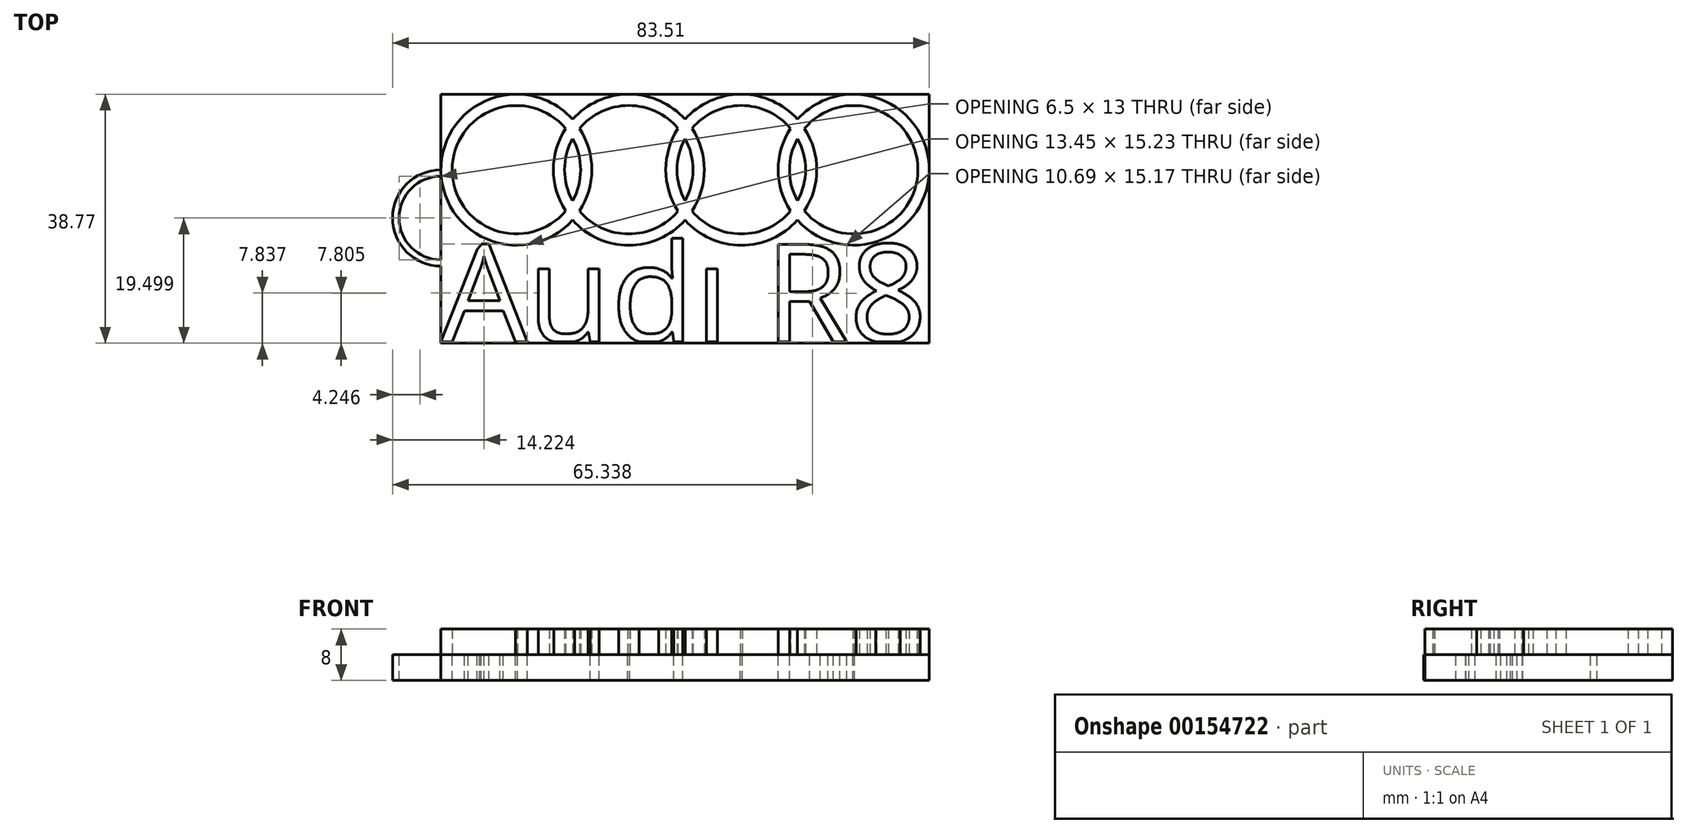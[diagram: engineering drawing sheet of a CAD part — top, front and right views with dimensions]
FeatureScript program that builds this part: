
annotation { "Feature Type Name" : "Feature", "Feature Type Description" : "" }
export const myFeature = defineFeature(function(context is Context, id is Id, definition is map)
    precondition{}
    {
        {
            var Q0;
            Q0=qCreatedBy(makeId("Top.planeOp"),FACE);
            var sketch = newSketch(context, id + "F0", { "sketchPlane" : qUnion([Q0])});
            skCircle(sketch, "E0", {"center": v(-42.08, 0) * mm, "radius": 10 * mm});
            skCircle(sketch, "E1", {"center": v(-24.58, 0) * mm, "radius": 10 * mm});
            skCircle(sketch, "E2", {"center": v(-7.08, 0) * mm, "radius": 10 * mm});
            skCircle(sketch, "E3", {"center": v(10.42, 0) * mm, "radius": 10 * mm});
            skCircle(sketch, "E4", {"center": v(-42.08, 0) * mm, "radius": 11.75 * mm});
            skCircle(sketch, "E5", {"center": v(-24.58, 0) * mm, "radius": 11.75 * mm});
            skCircle(sketch, "E6", {"center": v(-7.08, 0) * mm, "radius": 11.75 * mm});
            skCircle(sketch, "E7", {"center": v(10.42, 0) * mm, "radius": 11.75 * mm});
            skPoint(sketch, "E8.startSnap0", {"position": v(78.32, -3.69) * mm});
            skLineSegment(sketch, "E9", {"start": v(-57.65, 0) * mm, "end": v(52.35, 0) * mm});
            skLineSegment(sketch, "E10.bottom", {"start": v(-53.84, 11.75) * mm, "end": v(22.17, 11.75) * mm});
            skLineSegment(sketch, "E10.top", {"start": v(-53.84, -26.8) * mm, "end": v(22.17, -26.8) * mm});
            skLineSegment(sketch, "E10.left", {"start": v(-53.84, 11.75) * mm, "end": v(-53.84, -26.8) * mm});
            skLineSegment(sketch, "E10.right", {"start": v(22.17, 11.75) * mm, "end": v(22.17, -26.8) * mm});
            skText(sketch, "E11", { "text": "Audi R8", "fontName": "OpenSans-Regular.ttf"});
            skLineSegment(sketch, "E12.top", {"start": v(-53.84, -27.02) * mm, "end": v(22.17, -27.02) * mm});
            skLineSegment(sketch, "E12.left", {"start": v(-53.84, -26.8) * mm, "end": v(-53.84, -27.02) * mm});
            skLineSegment(sketch, "E12.right", {"start": v(22.17, -26.8) * mm, "end": v(22.17, -27.02) * mm});
            skCircle(sketch, "E13", {"center": v(-53.84, -7.52) * mm, "radius": 7.5 * mm});
            skCircle(sketch, "E14", {"center": v(-53.84, -7.52) * mm, "radius": 6.5 * mm});
            const initialGuessF0  = {"E11": [-0.05384, -0.0268, 1, 0, 0.0153]};
            skSetInitialGuess(sketch, initialGuessF0);
            skSolve(sketch);
        }
        {
            var Q0;
            Q0 = qSketchRegion(id + "F0", true);
            var Q1;
            {var subQ5=sQuery(id+"F0.wireOp",EDGE,"E5");var subQ6=sQuery(id+"F0.wireOp",EDGE,"E0");var subQ7=makeQuery(id+"F0.imprint","INTERSECT",VERTEX,{"disambiguationData":[OD(0.0)],"derivedFrom":[subQ6,subQ5]});Q1=makeQuery(id+"F0.imprint","IMPRINT",FACE,{"disambiguationData":[TD([[makeQuery(id+"F0.imprint","IMPRINT",EDGE,{"disambiguationData":[TD([[subQ7,-1.0]])],"derivedFrom":subQ6}),-1.0]])]});}
            var Q2;
            {var subQ0=sQuery(id+"F0.wireOp",EDGE,"E11.sketch_text.stroke-0");Q2=makeQuery(id+"F0.imprint","IMPRINT",FACE,{"disambiguationData":[TD([[makeQuery(id+"F0.imprint","IMPRINT",EDGE,{"derivedFrom":subQ0}),1.0]])]});}
            var Q3;
            {var subQ7=sQuery(id+"F0.wireOp",EDGE,"E14");var subQ10=sQuery(id+"F0.wireOp",EDGE,"E4");var subQ11=makeQuery(id+"F0.imprint","INTERSECT",VERTEX,{"disambiguationData":[OD(1.0)],"derivedFrom":[subQ10,subQ7]});Q3=makeQuery(id+"F0.imprint","IMPRINT",FACE,{"disambiguationData":[TD([[makeQuery(id+"F0.imprint","IMPRINT",EDGE,{"disambiguationData":[TD([[subQ11,-1.0]])],"derivedFrom":subQ10}),-1.0]])]});}
            var Q4;
            Q4=makeQuery(id+"F0.imprint","IMPRINT",FACE,{"disambiguationData":[TD([[makeQuery(id+"F0.imprint","IMPRINT",EDGE,{"derivedFrom":sQuery(id+"F0.wireOp",EDGE,"E11.sketch_text.stroke-84")}),-1.0]])]});
            var Q5;
            {var subQ0=sQuery(id+"F0.wireOp",EDGE,"E9");var subQ1=sQuery(id+"F0.wireOp",EDGE,"E2");var subQ2=makeQuery(id+"F0.imprint","INTERSECT",VERTEX,{"disambiguationData":[OD(0.0)],"derivedFrom":[subQ1,subQ0]});Q5=makeQuery(id+"F0.imprint","IMPRINT",FACE,{"disambiguationData":[TD([[makeQuery(id+"F0.imprint","IMPRINT",EDGE,{"disambiguationData":[TD([[subQ2,1.0]])],"derivedFrom":subQ1}),-1.0]])]});}
            var Q6;
            {var subQ0=sQuery(id+"F0.wireOp",EDGE,"E5");var subQ1=sQuery(id+"F0.wireOp",EDGE,"E0");var subQ2=makeQuery(id+"F0.imprint","INTERSECT",VERTEX,{"disambiguationData":[OD(1.0)],"derivedFrom":[subQ1,subQ0]});Q6=makeQuery(id+"F0.imprint","IMPRINT",FACE,{"disambiguationData":[TD([[makeQuery(id+"F0.imprint","IMPRINT",EDGE,{"disambiguationData":[TD([[subQ2,-1.0]])],"derivedFrom":subQ1}),-1.0]])]});}
            var Q7;
            {var subQ0=sQuery(id+"F0.wireOp",EDGE,"E3");var subQ1=sQuery(id+"F0.wireOp",EDGE,"E2");var subQ2=makeQuery(id+"F0.imprint","INTERSECT",VERTEX,{"disambiguationData":[OD(0.0)],"derivedFrom":[subQ1,subQ0]});Q7=makeQuery(id+"F0.imprint","IMPRINT",FACE,{"disambiguationData":[TD([[makeQuery(id+"F0.imprint","IMPRINT",EDGE,{"disambiguationData":[TD([[subQ2,1.0]])],"derivedFrom":subQ1}),1.0]])]});}
            var Q8;
            {var subQ0=sQuery(id+"F0.wireOp",EDGE,"E7");var subQ1=sQuery(id+"F0.wireOp",EDGE,"E2");var subQ2=makeQuery(id+"F0.imprint","INTERSECT",VERTEX,{"disambiguationData":[OD(1.0)],"derivedFrom":[subQ1,subQ0]});Q8=makeQuery(id+"F0.imprint","IMPRINT",FACE,{"disambiguationData":[TD([[makeQuery(id+"F0.imprint","IMPRINT",EDGE,{"disambiguationData":[TD([[subQ2,-1.0]])],"derivedFrom":subQ1}),1.0]])]});}
            var Q9;
            {var subQ0=sQuery(id+"F0.wireOp",EDGE,"E3");var subQ1=sQuery(id+"F0.wireOp",EDGE,"E2");var subQ2=makeQuery(id+"F0.imprint","INTERSECT",VERTEX,{"disambiguationData":[OD(0.0)],"derivedFrom":[subQ1,subQ0]});Q9=makeQuery(id+"F0.imprint","IMPRINT",FACE,{"disambiguationData":[TD([[makeQuery(id+"F0.imprint","IMPRINT",EDGE,{"disambiguationData":[TD([[subQ2,-1.0]])],"derivedFrom":subQ1}),-1.0]])]});}
            var Q10;
            {var subQ0=sQuery(id+"F0.wireOp",EDGE,"E14");var subQ1=sQuery(id+"F0.wireOp",EDGE,"E0");var subQ2=makeQuery(id+"F0.imprint","INTERSECT",VERTEX,{"disambiguationData":[OD(0.0)],"derivedFrom":[subQ1,subQ0]});Q10=makeQuery(id+"F0.imprint","IMPRINT",FACE,{"disambiguationData":[TD([[makeQuery(id+"F0.imprint","IMPRINT",EDGE,{"disambiguationData":[TD([[subQ2,-1.0]])],"derivedFrom":subQ1}),-1.0]])]});}
            var Q11;
            {var subQ0=sQuery(id+"F0.wireOp",EDGE,"E9");var subQ1=sQuery(id+"F0.wireOp",EDGE,"E1");var subQ2=makeQuery(id+"F0.imprint","INTERSECT",VERTEX,{"disambiguationData":[OD(0.0)],"derivedFrom":[subQ1,subQ0]});Q11=makeQuery(id+"F0.imprint","IMPRINT",FACE,{"disambiguationData":[TD([[makeQuery(id+"F0.imprint","IMPRINT",EDGE,{"disambiguationData":[TD([[subQ2,1.0]])],"derivedFrom":subQ1}),-1.0]])]});}
            var Q12;
            {var subQ0=sQuery(id+"F0.wireOp",EDGE,"E1");var subQ1=sQuery(id+"F0.wireOp",EDGE,"E0");var subQ2=makeQuery(id+"F0.imprint","INTERSECT",VERTEX,{"disambiguationData":[OD(0.0)],"derivedFrom":[subQ1,subQ0]});Q12=makeQuery(id+"F0.imprint","IMPRINT",FACE,{"disambiguationData":[TD([[makeQuery(id+"F0.imprint","IMPRINT",EDGE,{"disambiguationData":[TD([[subQ2,1.0]])],"derivedFrom":subQ1}),-1.0]])]});}
            var Q13;
            Q13=makeQuery(id+"F0.imprint","IMPRINT",FACE,{"disambiguationData":[TD([[makeQuery(id+"F0.imprint","IMPRINT",EDGE,{"derivedFrom":sQuery(id+"F0.wireOp",EDGE,"E11.sketch_text.stroke-77")}),1.0]])]});
            var Q14;
            {var subQ0=sQuery(id+"F0.wireOp",EDGE,"E5");var subQ1=sQuery(id+"F0.wireOp",EDGE,"E2");var subQ2=makeQuery(id+"F0.imprint","INTERSECT",VERTEX,{"disambiguationData":[OD(1.0)],"derivedFrom":[subQ1,subQ0]});Q14=makeQuery(id+"F0.imprint","IMPRINT",FACE,{"disambiguationData":[TD([[makeQuery(id+"F0.imprint","IMPRINT",EDGE,{"disambiguationData":[TD([[subQ2,-1.0]])],"derivedFrom":subQ1}),1.0]])]});}
            var Q15;
            {var subQ0=sQuery(id+"F0.wireOp",EDGE,"E9");var subQ1=sQuery(id+"F0.wireOp",EDGE,"E0");var subQ2=makeQuery(id+"F0.imprint","INTERSECT",VERTEX,{"disambiguationData":[OD(0.0)],"derivedFrom":[subQ1,subQ0]});Q15=makeQuery(id+"F0.imprint","IMPRINT",FACE,{"disambiguationData":[TD([[makeQuery(id+"F0.imprint","IMPRINT",EDGE,{"disambiguationData":[TD([[subQ2,1.0]])],"derivedFrom":subQ1}),-1.0]])]});}
            var Q16;
            {var subQ0=sQuery(id+"F0.wireOp",EDGE,"E3");var subQ1=sQuery(id+"F0.wireOp",EDGE,"E2");var subQ2=makeQuery(id+"F0.imprint","INTERSECT",VERTEX,{"disambiguationData":[OD(0.0)],"derivedFrom":[subQ1,subQ0]});Q16=makeQuery(id+"F0.imprint","IMPRINT",FACE,{"disambiguationData":[TD([[makeQuery(id+"F0.imprint","IMPRINT",EDGE,{"disambiguationData":[TD([[subQ2,1.0]])],"derivedFrom":subQ1}),-1.0]])]});}
            var Q17;
            {var subQ0=sQuery(id+"F0.wireOp",EDGE,"E1");var subQ1=sQuery(id+"F0.wireOp",EDGE,"E0");var subQ2=makeQuery(id+"F0.imprint","INTERSECT",VERTEX,{"disambiguationData":[OD(0.0)],"derivedFrom":[subQ1,subQ0]});Q17=makeQuery(id+"F0.imprint","IMPRINT",FACE,{"disambiguationData":[TD([[makeQuery(id+"F0.imprint","IMPRINT",EDGE,{"disambiguationData":[TD([[subQ2,-1.0]])],"derivedFrom":subQ1}),-1.0]])]});}
            var Q18;
            {var subQ0=sQuery(id+"F0.wireOp",EDGE,"E2");var subQ1=sQuery(id+"F0.wireOp",EDGE,"E1");var subQ2=makeQuery(id+"F0.imprint","INTERSECT",VERTEX,{"disambiguationData":[OD(0.0)],"derivedFrom":[subQ1,subQ0]});Q18=makeQuery(id+"F0.imprint","IMPRINT",FACE,{"disambiguationData":[TD([[makeQuery(id+"F0.imprint","IMPRINT",EDGE,{"disambiguationData":[TD([[subQ2,1.0]])],"derivedFrom":subQ1}),1.0]])]});}
            var Q19;
            {var subQ0=sQuery(id+"F0.wireOp",EDGE,"E9");var subQ1=sQuery(id+"F0.wireOp",EDGE,"E2");var subQ2=makeQuery(id+"F0.imprint","INTERSECT",VERTEX,{"disambiguationData":[OD(0.0)],"derivedFrom":[subQ1,subQ0]});Q19=makeQuery(id+"F0.imprint","IMPRINT",FACE,{"disambiguationData":[TD([[makeQuery(id+"F0.imprint","IMPRINT",EDGE,{"disambiguationData":[TD([[subQ2,1.0]])],"derivedFrom":subQ1}),1.0]])]});}
            var Q20;
            Q20=makeQuery(id+"F0.imprint","IMPRINT",FACE,{"disambiguationData":[TD([[makeQuery(id+"F0.imprint","IMPRINT",EDGE,{"derivedFrom":sQuery(id+"F0.wireOp",EDGE,"E11.sketch_text.stroke-99")}),1.0]])]});
            var Q21;
            {var subQ0=sQuery(id+"F0.wireOp",EDGE,"E13");var subQ1=sQuery(id+"F0.wireOp",EDGE,"E10.left");var subQ2=makeQuery(id+"F0.imprint","INTERSECT",VERTEX,{"disambiguationData":[OD(0.0)],"derivedFrom":[subQ1,subQ0]});Q21=makeQuery(id+"F0.imprint","IMPRINT",FACE,{"disambiguationData":[TD([[makeQuery(id+"F0.imprint","IMPRINT",EDGE,{"disambiguationData":[TD([[subQ2,-1.0]])],"derivedFrom":subQ1}),-1.0]])]});}
            var Q22;
            Q22=makeQuery(id+"F0.imprint","IMPRINT",FACE,{"disambiguationData":[TD([[makeQuery(id+"F0.imprint","IMPRINT",EDGE,{"derivedFrom":sQuery(id+"F0.wireOp",EDGE,"E11.sketch_text.stroke-58")}),-1.0]])]});
            var Q23;
            {var subQ0=sQuery(id+"F0.wireOp",EDGE,"E11.sketch_text.stroke-55");Q23=makeQuery(id+"F0.imprint","IMPRINT",FACE,{"disambiguationData":[TD([[makeQuery(id+"F0.imprint","IMPRINT",EDGE,{"derivedFrom":subQ0}),-1.0]])]});}
            var Q24;
            {var subQ0=sQuery(id+"F0.wireOp",EDGE,"E9");var subQ1=sQuery(id+"F0.wireOp",EDGE,"E3");var subQ2=makeQuery(id+"F0.imprint","INTERSECT",VERTEX,{"disambiguationData":[OD(0.0)],"derivedFrom":[subQ1,subQ0]});Q24=makeQuery(id+"F0.imprint","IMPRINT",FACE,{"disambiguationData":[TD([[makeQuery(id+"F0.imprint","IMPRINT",EDGE,{"disambiguationData":[TD([[subQ2,1.0]])],"derivedFrom":subQ1}),-1.0]])]});}
            var Q25;
            {var subQ0=sQuery(id+"F0.wireOp",EDGE,"E2");var subQ1=sQuery(id+"F0.wireOp",EDGE,"E1");var subQ2=makeQuery(id+"F0.imprint","INTERSECT",VERTEX,{"disambiguationData":[OD(0.0)],"derivedFrom":[subQ1,subQ0]});Q25=makeQuery(id+"F0.imprint","IMPRINT",FACE,{"disambiguationData":[TD([[makeQuery(id+"F0.imprint","IMPRINT",EDGE,{"disambiguationData":[TD([[subQ2,-1.0]])],"derivedFrom":subQ1}),1.0]])]});}
            var Q26;
            {var subQ2=sQuery(id+"F0.wireOp",EDGE,"E11.sketch_text.stroke-30");Q26=makeQuery(id+"F0.imprint","IMPRINT",FACE,{"disambiguationData":[TD([[makeQuery(id+"F0.imprint","IMPRINT",EDGE,{"derivedFrom":subQ2}),-1.0]])]});}
            var Q27;
            {var subQ0=sQuery(id+"F0.wireOp",EDGE,"E9");var subQ1=sQuery(id+"F0.wireOp",EDGE,"E0");var subQ2=makeQuery(id+"F0.imprint","INTERSECT",VERTEX,{"disambiguationData":[OD(0.0)],"derivedFrom":[subQ1,subQ0]});Q27=makeQuery(id+"F0.imprint","IMPRINT",FACE,{"disambiguationData":[TD([[makeQuery(id+"F0.imprint","IMPRINT",EDGE,{"disambiguationData":[TD([[subQ2,1.0]])],"derivedFrom":subQ1}),1.0]])]});}
            var Q28;
            {var subQ0=sQuery(id+"F0.wireOp",EDGE,"E6");var subQ1=sQuery(id+"F0.wireOp",EDGE,"E3");var subQ2=makeQuery(id+"F0.imprint","INTERSECT",VERTEX,{"disambiguationData":[OD(0.0)],"derivedFrom":[subQ1,subQ0]});Q28=makeQuery(id+"F0.imprint","IMPRINT",FACE,{"disambiguationData":[TD([[makeQuery(id+"F0.imprint","IMPRINT",EDGE,{"disambiguationData":[TD([[subQ2,1.0]])],"derivedFrom":subQ1}),1.0]])]});}
            var Q29;
            {var subQ0=sQuery(id+"F0.wireOp",EDGE,"E14");var subQ1=sQuery(id+"F0.wireOp",EDGE,"E0");var subQ2=makeQuery(id+"F0.imprint","INTERSECT",VERTEX,{"disambiguationData":[OD(1.0)],"derivedFrom":[subQ1,subQ0]});Q29=makeQuery(id+"F0.imprint","IMPRINT",FACE,{"disambiguationData":[TD([[makeQuery(id+"F0.imprint","IMPRINT",EDGE,{"disambiguationData":[TD([[subQ2,-1.0]])],"derivedFrom":subQ1}),-1.0]])]});}
            var Q30;
            {var subQ0=sQuery(id+"F0.wireOp",EDGE,"E5");var subQ1=sQuery(id+"F0.wireOp",EDGE,"E0");var subQ2=makeQuery(id+"F0.imprint","INTERSECT",VERTEX,{"disambiguationData":[OD(1.0)],"derivedFrom":[subQ1,subQ0]});Q30=makeQuery(id+"F0.imprint","IMPRINT",FACE,{"disambiguationData":[TD([[makeQuery(id+"F0.imprint","IMPRINT",EDGE,{"disambiguationData":[TD([[subQ2,-1.0]])],"derivedFrom":subQ1}),1.0]])]});}
            var Q31;
            {var subQ0=sQuery(id+"F0.wireOp",EDGE,"E5");var subQ1=sQuery(id+"F0.wireOp",EDGE,"E0");var subQ2=makeQuery(id+"F0.imprint","INTERSECT",VERTEX,{"disambiguationData":[OD(0.0)],"derivedFrom":[subQ1,subQ0]});Q31=makeQuery(id+"F0.imprint","IMPRINT",FACE,{"disambiguationData":[TD([[makeQuery(id+"F0.imprint","IMPRINT",EDGE,{"disambiguationData":[TD([[subQ2,-1.0]])],"derivedFrom":subQ1}),1.0]])]});}
            var Q32;
            {var subQ1=sQuery(id+"F0.wireOp",EDGE,"E10.left");var subQ3=sQuery(id+"F0.wireOp",EDGE,"E13");var subQ4=makeQuery(id+"F0.imprint","INTERSECT",VERTEX,{"disambiguationData":[OD(1.0)],"derivedFrom":[subQ1,subQ3]});Q32=makeQuery(id+"F0.imprint","IMPRINT",FACE,{"disambiguationData":[TD([[makeQuery(id+"F0.imprint","IMPRINT",EDGE,{"disambiguationData":[TD([[subQ4,-1.0]])],"derivedFrom":subQ3}),-1.0]])]});}
            var Q33;
            {var subQ0=sQuery(id+"F0.wireOp",EDGE,"E2");var subQ1=sQuery(id+"F0.wireOp",EDGE,"E1");var subQ2=makeQuery(id+"F0.imprint","INTERSECT",VERTEX,{"disambiguationData":[OD(0.0)],"derivedFrom":[subQ1,subQ0]});Q33=makeQuery(id+"F0.imprint","IMPRINT",FACE,{"disambiguationData":[TD([[makeQuery(id+"F0.imprint","IMPRINT",EDGE,{"disambiguationData":[TD([[subQ2,1.0]])],"derivedFrom":subQ1}),-1.0]])]});}
            var Q34;
            {var subQ0=sQuery(id+"F0.wireOp",EDGE,"E9");var subQ1=sQuery(id+"F0.wireOp",EDGE,"E3");var subQ2=makeQuery(id+"F0.imprint","INTERSECT",VERTEX,{"disambiguationData":[OD(0.0)],"derivedFrom":[subQ1,subQ0]});Q34=makeQuery(id+"F0.imprint","IMPRINT",FACE,{"disambiguationData":[TD([[makeQuery(id+"F0.imprint","IMPRINT",EDGE,{"disambiguationData":[TD([[subQ2,1.0]])],"derivedFrom":subQ1}),1.0]])]});}
            var Q35;
            {var subQ0=sQuery(id+"F0.wireOp",EDGE,"E14");var subQ1=sQuery(id+"F0.wireOp",EDGE,"E4");var subQ2=makeQuery(id+"F0.imprint","INTERSECT",VERTEX,{"disambiguationData":[OD(0.0)],"derivedFrom":[subQ1,subQ0]});Q35=makeQuery(id+"F0.imprint","IMPRINT",FACE,{"disambiguationData":[TD([[makeQuery(id+"F0.imprint","IMPRINT",EDGE,{"disambiguationData":[TD([[subQ2,-1.0]])],"derivedFrom":subQ1}),-1.0]])]});}
            var Q36;
            {var subQ0=sQuery(id+"F0.wireOp",EDGE,"E13");var subQ1=sQuery(id+"F0.wireOp",EDGE,"E0");var subQ2=makeQuery(id+"F0.imprint","INTERSECT",VERTEX,{"disambiguationData":[OD(0.0)],"derivedFrom":[subQ1,subQ0]});Q36=makeQuery(id+"F0.imprint","IMPRINT",FACE,{"disambiguationData":[TD([[makeQuery(id+"F0.imprint","IMPRINT",EDGE,{"disambiguationData":[TD([[subQ2,-1.0]])],"derivedFrom":subQ1}),1.0]])]});}
            var Q37;
            {var subQ0=sQuery(id+"F0.wireOp",EDGE,"E1");var subQ1=sQuery(id+"F0.wireOp",EDGE,"E0");var subQ2=makeQuery(id+"F0.imprint","INTERSECT",VERTEX,{"disambiguationData":[OD(0.0)],"derivedFrom":[subQ1,subQ0]});Q37=makeQuery(id+"F0.imprint","IMPRINT",FACE,{"disambiguationData":[TD([[makeQuery(id+"F0.imprint","IMPRINT",EDGE,{"disambiguationData":[TD([[subQ2,1.0]])],"derivedFrom":subQ1}),1.0]])]});}
            var Q38;
            Q38=makeQuery(id+"F0.imprint","IMPRINT",FACE,{"disambiguationData":[TD([[makeQuery(id+"F0.imprint","IMPRINT",EDGE,{"derivedFrom":sQuery(id+"F0.wireOp",EDGE,"E11.sketch_text.stroke-107")}),1.0]])]});
            var Q39;
            Q39=makeQuery(id+"F0.imprint","IMPRINT",FACE,{"disambiguationData":[TD([[makeQuery(id+"F0.imprint","IMPRINT",EDGE,{"derivedFrom":sQuery(id+"F0.wireOp",EDGE,"E11.sketch_text.stroke-45")}),1.0]])]});
            var Q40;
            {var subQ0=sQuery(id+"F0.wireOp",EDGE,"E6");var subQ1=sQuery(id+"F0.wireOp",EDGE,"E3");var subQ2=makeQuery(id+"F0.imprint","INTERSECT",VERTEX,{"disambiguationData":[OD(0.0)],"derivedFrom":[subQ1,subQ0]});Q40=makeQuery(id+"F0.imprint","IMPRINT",FACE,{"disambiguationData":[TD([[makeQuery(id+"F0.imprint","IMPRINT",EDGE,{"disambiguationData":[TD([[subQ2,1.0]])],"derivedFrom":subQ1}),-1.0]])]});}
            var Q41;
            {var subQ0=sQuery(id+"F0.wireOp",EDGE,"E4");var subQ1=sQuery(id+"F0.wireOp",EDGE,"E1");var subQ2=makeQuery(id+"F0.imprint","INTERSECT",VERTEX,{"disambiguationData":[OD(1.0)],"derivedFrom":[subQ1,subQ0]});Q41=makeQuery(id+"F0.imprint","IMPRINT",FACE,{"disambiguationData":[TD([[makeQuery(id+"F0.imprint","IMPRINT",EDGE,{"disambiguationData":[TD([[subQ2,-1.0]])],"derivedFrom":subQ1}),1.0]])]});}
            var Q42;
            {var subQ0=sQuery(id+"F0.wireOp",EDGE,"E7");var subQ1=sQuery(id+"F0.wireOp",EDGE,"E2");var subQ2=makeQuery(id+"F0.imprint","INTERSECT",VERTEX,{"disambiguationData":[OD(1.0)],"derivedFrom":[subQ1,subQ0]});Q42=makeQuery(id+"F0.imprint","IMPRINT",FACE,{"disambiguationData":[TD([[makeQuery(id+"F0.imprint","IMPRINT",EDGE,{"disambiguationData":[TD([[subQ2,-1.0]])],"derivedFrom":subQ1}),-1.0]])]});}
            var Q43;
            {var subQ0=sQuery(id+"F0.wireOp",EDGE,"E6");var subQ1=sQuery(id+"F0.wireOp",EDGE,"E1");var subQ2=makeQuery(id+"F0.imprint","INTERSECT",VERTEX,{"disambiguationData":[OD(1.0)],"derivedFrom":[subQ1,subQ0]});Q43=makeQuery(id+"F0.imprint","IMPRINT",FACE,{"disambiguationData":[TD([[makeQuery(id+"F0.imprint","IMPRINT",EDGE,{"disambiguationData":[TD([[subQ2,-1.0]])],"derivedFrom":subQ1}),-1.0]])]});}
            var Q44;
            {var subQ0=sQuery(id+"F0.wireOp",EDGE,"E5");var subQ1=sQuery(id+"F0.wireOp",EDGE,"E2");var subQ2=makeQuery(id+"F0.imprint","INTERSECT",VERTEX,{"disambiguationData":[OD(1.0)],"derivedFrom":[subQ1,subQ0]});Q44=makeQuery(id+"F0.imprint","IMPRINT",FACE,{"disambiguationData":[TD([[makeQuery(id+"F0.imprint","IMPRINT",EDGE,{"disambiguationData":[TD([[subQ2,-1.0]])],"derivedFrom":subQ1}),-1.0]])]});}
            var Q45;
            {var subQ4=sQuery(id+"F0.wireOp",EDGE,"E11.sketch_text.stroke-22");Q45=makeQuery(id+"F0.imprint","IMPRINT",FACE,{"disambiguationData":[TD([[makeQuery(id+"F0.imprint","IMPRINT",EDGE,{"derivedFrom":subQ4}),1.0]])]});}
            var Q46;
            {var subQ0=sQuery(id+"F0.wireOp",EDGE,"E13");var subQ1=sQuery(id+"F0.wireOp",EDGE,"E0");var subQ2=makeQuery(id+"F0.imprint","INTERSECT",VERTEX,{"disambiguationData":[OD(1.0)],"derivedFrom":[subQ1,subQ0]});Q46=makeQuery(id+"F0.imprint","IMPRINT",FACE,{"disambiguationData":[TD([[makeQuery(id+"F0.imprint","IMPRINT",EDGE,{"disambiguationData":[TD([[subQ2,-1.0]])],"derivedFrom":subQ1}),-1.0]])]});}
            var Q47;
            {var subQ0=sQuery(id+"F0.wireOp",EDGE,"E10.bottom");var subQ1=sQuery(id+"F0.wireOp",EDGE,"E7");var subQ2=makeQuery(id+"F0.imprint","INTERSECT",VERTEX,{"disambiguationData":[OD(0.0)],"derivedFrom":[subQ1,subQ0]});Q47=makeQuery(id+"F0.imprint","IMPRINT",FACE,{"disambiguationData":[TD([[makeQuery(id+"F0.imprint","IMPRINT",EDGE,{"disambiguationData":[TD([[subQ2,1.0]])],"derivedFrom":subQ1}),-1.0]])]});}
            var Q48;
            {var subQ0=sQuery(id+"F0.wireOp",EDGE,"E14");var subQ1=sQuery(id+"F0.wireOp",EDGE,"E0");var subQ2=makeQuery(id+"F0.imprint","INTERSECT",VERTEX,{"disambiguationData":[OD(0.0)],"derivedFrom":[subQ1,subQ0]});Q48=makeQuery(id+"F0.imprint","IMPRINT",FACE,{"disambiguationData":[TD([[makeQuery(id+"F0.imprint","IMPRINT",EDGE,{"disambiguationData":[TD([[subQ2,-1.0]])],"derivedFrom":subQ1}),1.0]])]});}
            var Q49;
            {var subQ0=sQuery(id+"F0.wireOp",EDGE,"E3");var subQ1=sQuery(id+"F0.wireOp",EDGE,"E2");var subQ2=makeQuery(id+"F0.imprint","INTERSECT",VERTEX,{"disambiguationData":[OD(0.0)],"derivedFrom":[subQ1,subQ0]});Q49=makeQuery(id+"F0.imprint","IMPRINT",FACE,{"disambiguationData":[TD([[makeQuery(id+"F0.imprint","IMPRINT",EDGE,{"disambiguationData":[TD([[subQ2,-1.0]])],"derivedFrom":subQ1}),1.0]])]});}
            var Q50;
            {var subQ0=sQuery(id+"F0.wireOp",EDGE,"E6");var subQ1=sQuery(id+"F0.wireOp",EDGE,"E1");var subQ2=makeQuery(id+"F0.imprint","INTERSECT",VERTEX,{"disambiguationData":[OD(0.0)],"derivedFrom":[subQ1,subQ0]});Q50=makeQuery(id+"F0.imprint","IMPRINT",FACE,{"disambiguationData":[TD([[makeQuery(id+"F0.imprint","IMPRINT",EDGE,{"disambiguationData":[TD([[subQ2,-1.0]])],"derivedFrom":subQ1}),1.0]])]});}
            var Q51;
            {var subQ0=sQuery(id+"F0.wireOp",EDGE,"E11.sketch_text.stroke-66");Q51=makeQuery(id+"F0.imprint","IMPRINT",FACE,{"disambiguationData":[TD([[makeQuery(id+"F0.imprint","IMPRINT",EDGE,{"derivedFrom":subQ0}),1.0]])]});}
            var Q52;
            {var subQ0=sQuery(id+"F0.wireOp",EDGE,"E7");var subQ1=sQuery(id+"F0.wireOp",EDGE,"E2");var subQ2=makeQuery(id+"F0.imprint","INTERSECT",VERTEX,{"disambiguationData":[OD(0.0)],"derivedFrom":[subQ1,subQ0]});Q52=makeQuery(id+"F0.imprint","IMPRINT",FACE,{"disambiguationData":[TD([[makeQuery(id+"F0.imprint","IMPRINT",EDGE,{"disambiguationData":[TD([[subQ2,-1.0]])],"derivedFrom":subQ1}),1.0]])]});}
            var Q53;
            {var subQ0=sQuery(id+"F0.wireOp",EDGE,"E6");var subQ1=sQuery(id+"F0.wireOp",EDGE,"E1");var subQ2=makeQuery(id+"F0.imprint","INTERSECT",VERTEX,{"disambiguationData":[OD(1.0)],"derivedFrom":[subQ1,subQ0]});Q53=makeQuery(id+"F0.imprint","IMPRINT",FACE,{"disambiguationData":[TD([[makeQuery(id+"F0.imprint","IMPRINT",EDGE,{"disambiguationData":[TD([[subQ2,-1.0]])],"derivedFrom":subQ1}),1.0]])]});}
            var Q54;
            {var subQ0=sQuery(id+"F0.wireOp",EDGE,"E9");var subQ1=sQuery(id+"F0.wireOp",EDGE,"E1");var subQ2=makeQuery(id+"F0.imprint","INTERSECT",VERTEX,{"disambiguationData":[OD(0.0)],"derivedFrom":[subQ1,subQ0]});Q54=makeQuery(id+"F0.imprint","IMPRINT",FACE,{"disambiguationData":[TD([[makeQuery(id+"F0.imprint","IMPRINT",EDGE,{"disambiguationData":[TD([[subQ2,1.0]])],"derivedFrom":subQ1}),1.0]])]});}
            var Q55;
            {var subQ0=sQuery(id+"F0.wireOp",EDGE,"E1");var subQ1=sQuery(id+"F0.wireOp",EDGE,"E0");var subQ2=makeQuery(id+"F0.imprint","INTERSECT",VERTEX,{"disambiguationData":[OD(0.0)],"derivedFrom":[subQ1,subQ0]});Q55=makeQuery(id+"F0.imprint","IMPRINT",FACE,{"disambiguationData":[TD([[makeQuery(id+"F0.imprint","IMPRINT",EDGE,{"disambiguationData":[TD([[subQ2,-1.0]])],"derivedFrom":subQ1}),1.0]])]});}
            var Q56;
            {var subQ0=sQuery(id+"F0.wireOp",EDGE,"E10.bottom");var subQ1=sQuery(id+"F0.wireOp",EDGE,"E6");var subQ2=makeQuery(id+"F0.imprint","INTERSECT",VERTEX,{"disambiguationData":[OD(0.0)],"derivedFrom":[subQ1,subQ0]});Q56=makeQuery(id+"F0.imprint","IMPRINT",FACE,{"disambiguationData":[TD([[makeQuery(id+"F0.imprint","IMPRINT",EDGE,{"disambiguationData":[TD([[subQ2,1.0]])],"derivedFrom":subQ1}),-1.0]])]});}
            var Q57;
            {var subQ0=sQuery(id+"F0.wireOp",EDGE,"E13");var subQ1=sQuery(id+"F0.wireOp",EDGE,"E0");var subQ2=makeQuery(id+"F0.imprint","INTERSECT",VERTEX,{"disambiguationData":[OD(0.0)],"derivedFrom":[subQ1,subQ0]});Q57=makeQuery(id+"F0.imprint","IMPRINT",FACE,{"disambiguationData":[TD([[makeQuery(id+"F0.imprint","IMPRINT",EDGE,{"disambiguationData":[TD([[subQ2,-1.0]])],"derivedFrom":subQ1}),-1.0]])]});}
            var Q58;
            {var subQ5=sQuery(id+"F0.wireOp",EDGE,"E11.sketch_text.stroke-0");Q58=makeQuery(id+"F0.imprint","IMPRINT",FACE,{"disambiguationData":[TD([[makeQuery(id+"F0.imprint","IMPRINT",EDGE,{"derivedFrom":subQ5}),-1.0]])]});}
            var Q59;
            Q59=makeQuery(id+"F0.imprint","IMPRINT",FACE,{"disambiguationData":[TD([[makeQuery(id+"F0.imprint","IMPRINT",EDGE,{"derivedFrom":sQuery(id+"F0.wireOp",EDGE,"E11.sketch_text.stroke-8")}),1.0]])]});
            var Q60;
            {var subQ3=sQuery(id+"F0.wireOp",EDGE,"E7");var subQ5=sQuery(id+"F0.wireOp",EDGE,"E2");var subQ6=makeQuery(id+"F0.imprint","INTERSECT",VERTEX,{"disambiguationData":[OD(0.0)],"derivedFrom":[subQ5,subQ3]});Q60=makeQuery(id+"F0.imprint","IMPRINT",FACE,{"disambiguationData":[TD([[makeQuery(id+"F0.imprint","IMPRINT",EDGE,{"disambiguationData":[TD([[subQ6,-1.0]])],"derivedFrom":subQ5}),-1.0]])]});}
            var Q61;
            {var subQ0=sQuery(id+"F0.wireOp",EDGE,"E4");var subQ1=sQuery(id+"F0.wireOp",EDGE,"E1");var subQ2=makeQuery(id+"F0.imprint","INTERSECT",VERTEX,{"disambiguationData":[OD(1.0)],"derivedFrom":[subQ1,subQ0]});Q61=makeQuery(id+"F0.imprint","IMPRINT",FACE,{"disambiguationData":[TD([[makeQuery(id+"F0.imprint","IMPRINT",EDGE,{"disambiguationData":[TD([[subQ2,-1.0]])],"derivedFrom":subQ1}),-1.0]])]});}
            var Q62;
            {var subQ6=sQuery(id+"F0.wireOp",EDGE,"E6");var subQ8=sQuery(id+"F0.wireOp",EDGE,"E1");var subQ10=makeQuery(id+"F0.imprint","INTERSECT",VERTEX,{"disambiguationData":[OD(0.0)],"derivedFrom":[subQ8,subQ6]});Q62=makeQuery(id+"F0.imprint","IMPRINT",FACE,{"disambiguationData":[TD([[makeQuery(id+"F0.imprint","IMPRINT",EDGE,{"disambiguationData":[TD([[subQ10,-1.0]])],"derivedFrom":subQ8}),-1.0]])]});}
            var Q63;
            {var subQ0=sQuery(id+"F0.wireOp",EDGE,"E2");var subQ1=sQuery(id+"F0.wireOp",EDGE,"E1");var subQ2=makeQuery(id+"F0.imprint","INTERSECT",VERTEX,{"disambiguationData":[OD(0.0)],"derivedFrom":[subQ1,subQ0]});Q63=makeQuery(id+"F0.imprint","IMPRINT",FACE,{"disambiguationData":[TD([[makeQuery(id+"F0.imprint","IMPRINT",EDGE,{"disambiguationData":[TD([[subQ2,-1.0]])],"derivedFrom":subQ1}),-1.0]])]});}
            var Q64;
            {var subQ0=sQuery(id+"F0.wireOp",EDGE,"E10.bottom");var subQ1=sQuery(id+"F0.wireOp",EDGE,"E5");var subQ2=makeQuery(id+"F0.imprint","INTERSECT",VERTEX,{"disambiguationData":[OD(0.0)],"derivedFrom":[subQ1,subQ0]});Q64=makeQuery(id+"F0.imprint","IMPRINT",FACE,{"disambiguationData":[TD([[makeQuery(id+"F0.imprint","IMPRINT",EDGE,{"disambiguationData":[TD([[subQ2,1.0]])],"derivedFrom":subQ1}),-1.0]])]});}
            var Q65;
            {var subQ0=sQuery(id+"F0.wireOp",EDGE,"E11.sketch_text.stroke-30");Q65=makeQuery(id+"F0.imprint","IMPRINT",FACE,{"disambiguationData":[TD([[makeQuery(id+"F0.imprint","IMPRINT",EDGE,{"derivedFrom":subQ0}),1.0]])]});}
            var Q66;
            {var subQ0=sQuery(id+"F0.wireOp",EDGE,"E10.bottom");var subQ1=sQuery(id+"F0.wireOp",EDGE,"E4");var subQ2=makeQuery(id+"F0.imprint","INTERSECT",VERTEX,{"disambiguationData":[OD(1.0)],"derivedFrom":[subQ1,subQ0]});Q66=makeQuery(id+"F0.imprint","IMPRINT",FACE,{"disambiguationData":[TD([[makeQuery(id+"F0.imprint","IMPRINT",EDGE,{"disambiguationData":[TD([[subQ2,-1.0]])],"derivedFrom":subQ1}),-1.0]])]});}
            var Q67;
            {var subQ0=sQuery(id+"F0.wireOp",EDGE,"E9");var subQ1=sQuery(id+"F0.wireOp",EDGE,"E0");var subQ2=makeQuery(id+"F0.imprint","INTERSECT",VERTEX,{"disambiguationData":[OD(1.0)],"derivedFrom":[subQ1,subQ0]});Q67=makeQuery(id+"F0.imprint","IMPRINT",FACE,{"disambiguationData":[TD([[makeQuery(id+"F0.imprint","IMPRINT",EDGE,{"disambiguationData":[TD([[subQ2,-1.0]])],"derivedFrom":subQ1}),1.0]])]});}
            var Q68;
            {var subQ3=sQuery(id+"F0.wireOp",EDGE,"E11.sketch_text.stroke-66");Q68=makeQuery(id+"F0.imprint","IMPRINT",FACE,{"disambiguationData":[TD([[makeQuery(id+"F0.imprint","IMPRINT",EDGE,{"derivedFrom":subQ3}),-1.0]])]});}
            var Q69;
            Q69=makeQuery(id+"F0.imprint","IMPRINT",FACE,{"disambiguationData":[TD([[makeQuery(id+"F0.imprint","IMPRINT",EDGE,{"derivedFrom":sQuery(id+"F0.wireOp",EDGE,"E11.sketch_text.stroke-13")}),-1.0]])]});
            var Q70;
            {var subQ18=sQuery(id+"F0.wireOp",EDGE,"E10.top");Q70=makeQuery(id+"F0.imprint","IMPRINT",FACE,{"disambiguationData":[TD([[makeQuery(id+"F0.imprint","IMPRINT",EDGE,{"derivedFrom":subQ18}),1.0]])]});}
            var Q71;
            {var subQ0=sQuery(id+"F0.wireOp",EDGE,"E10.bottom");var subQ1=sQuery(id+"F0.wireOp",EDGE,"E4");var subQ2=makeQuery(id+"F0.imprint","INTERSECT",VERTEX,{"disambiguationData":[OD(0.0)],"derivedFrom":[subQ1,subQ0]});Q71=makeQuery(id+"F0.imprint","IMPRINT",FACE,{"disambiguationData":[TD([[makeQuery(id+"F0.imprint","IMPRINT",EDGE,{"disambiguationData":[TD([[subQ2,1.0]])],"derivedFrom":subQ1}),-1.0]])]});}
            var Q72;
            {var subQ0=sQuery(id+"F0.wireOp",EDGE,"E11.sketch_text.stroke-5");var subQ1=sQuery(id+"F0.wireOp",EDGE,"E11.sketch_text.stroke-4");var subQ2=makeQuery(id+"F0.imprint","INTERSECT",VERTEX,{"derivedFrom":[subQ1,subQ0]});Q72=makeQuery(id+"F0.imprint","IMPRINT",FACE,{"disambiguationData":[TD([[makeQuery(id+"F0.imprint","IMPRINT",EDGE,{"disambiguationData":[TD([[subQ2,1.0]])],"derivedFrom":subQ1}),-1.0]])]});}
            var Q73;
            {var subQ0=sQuery(id+"F0.wireOp",EDGE,"E10.bottom");var subQ1=sQuery(id+"F0.wireOp",EDGE,"E6");var subQ2=makeQuery(id+"F0.imprint","INTERSECT",VERTEX,{"disambiguationData":[OD(0.0)],"derivedFrom":[subQ1,subQ0]});Q73=makeQuery(id+"F0.imprint","IMPRINT",FACE,{"disambiguationData":[TD([[makeQuery(id+"F0.imprint","IMPRINT",EDGE,{"disambiguationData":[TD([[subQ2,-1.0]])],"derivedFrom":subQ1}),1.0]])]});}
            var Q74;
            {var subQ0=sQuery(id+"F0.wireOp",EDGE,"E10.bottom");var subQ1=sQuery(id+"F0.wireOp",EDGE,"E7");var subQ2=makeQuery(id+"F0.imprint","INTERSECT",VERTEX,{"disambiguationData":[OD(0.0)],"derivedFrom":[subQ1,subQ0]});Q74=makeQuery(id+"F0.imprint","IMPRINT",FACE,{"disambiguationData":[TD([[makeQuery(id+"F0.imprint","IMPRINT",EDGE,{"disambiguationData":[TD([[subQ2,-1.0]])],"derivedFrom":subQ1}),1.0]])]});}
            var Q75;
            Q75=makeQuery(id+"F0.imprint","IMPRINT",FACE,{"disambiguationData":[TD([[makeQuery(id+"F0.imprint","IMPRINT",EDGE,{"derivedFrom":sQuery(id+"F0.wireOp",EDGE,"E12.top")}),1.0]])]});
            var Q76;
            {var subQ0=sQuery(id+"F0.wireOp",EDGE,"E10.bottom");var subQ1=sQuery(id+"F0.wireOp",EDGE,"E4");var subQ2=makeQuery(id+"F0.imprint","INTERSECT",VERTEX,{"disambiguationData":[OD(0.0)],"derivedFrom":[subQ1,subQ0]});Q76=makeQuery(id+"F0.imprint","IMPRINT",FACE,{"disambiguationData":[TD([[makeQuery(id+"F0.imprint","IMPRINT",EDGE,{"disambiguationData":[TD([[subQ2,-1.0]])],"derivedFrom":subQ1}),1.0]])]});}
            var Q77;
            {var subQ0=sQuery(id+"F0.wireOp",EDGE,"E9");var subQ1=sQuery(id+"F0.wireOp",EDGE,"E0");var subQ2=makeQuery(id+"F0.imprint","INTERSECT",VERTEX,{"disambiguationData":[OD(1.0)],"derivedFrom":[subQ1,subQ0]});Q77=makeQuery(id+"F0.imprint","IMPRINT",FACE,{"disambiguationData":[TD([[makeQuery(id+"F0.imprint","IMPRINT",EDGE,{"disambiguationData":[TD([[subQ2,-1.0]])],"derivedFrom":subQ1}),-1.0]])]});}
            var Q78;
            {var subQ0=sQuery(id+"F0.wireOp",EDGE,"E13");var subQ1=sQuery(id+"F0.wireOp",EDGE,"E4");var subQ2=makeQuery(id+"F0.imprint","INTERSECT",VERTEX,{"disambiguationData":[OD(0.0)],"derivedFrom":[subQ1,subQ0]});Q78=makeQuery(id+"F0.imprint","IMPRINT",FACE,{"disambiguationData":[TD([[makeQuery(id+"F0.imprint","IMPRINT",EDGE,{"disambiguationData":[TD([[subQ2,-1.0]])],"derivedFrom":subQ1}),-1.0]])]});}
            var Q79;
            {var subQ0=sQuery(id+"F0.wireOp",EDGE,"E10.bottom");var subQ1=sQuery(id+"F0.wireOp",EDGE,"E5");var subQ2=makeQuery(id+"F0.imprint","INTERSECT",VERTEX,{"disambiguationData":[OD(0.0)],"derivedFrom":[subQ1,subQ0]});Q79=makeQuery(id+"F0.imprint","IMPRINT",FACE,{"disambiguationData":[TD([[makeQuery(id+"F0.imprint","IMPRINT",EDGE,{"disambiguationData":[TD([[subQ2,-1.0]])],"derivedFrom":subQ1}),1.0]])]});}
            var Q80;
            {var subQ0=sQuery(id+"F0.wireOp",EDGE,"E9");var subQ1=sQuery(id+"F0.wireOp",EDGE,"E4");var subQ2=makeQuery(id+"F0.imprint","INTERSECT",VERTEX,{"disambiguationData":[OD(1.0)],"derivedFrom":[subQ1,subQ0]});Q80=makeQuery(id+"F0.imprint","IMPRINT",FACE,{"disambiguationData":[TD([[makeQuery(id+"F0.imprint","IMPRINT",EDGE,{"disambiguationData":[TD([[subQ2,-1.0]])],"derivedFrom":subQ1}),-1.0]])]});}
            var Q81;
            {var subQ0=sQuery(id+"F0.wireOp",EDGE,"E11.sketch_text.stroke-92");var subQ1=sQuery(id+"F0.wireOp",EDGE,"E11.sketch_text.stroke-91");var subQ2=makeQuery(id+"F0.imprint","INTERSECT",VERTEX,{"derivedFrom":[subQ1,subQ0]});Q81=makeQuery(id+"F0.imprint","IMPRINT",FACE,{"disambiguationData":[TD([[makeQuery(id+"F0.imprint","IMPRINT",EDGE,{"disambiguationData":[TD([[subQ2,1.0]])],"derivedFrom":subQ1}),-1.0]])]});}
            var Q82;
            {var subQ0=sQuery(id+"F0.wireOp",EDGE,"E11.sketch_text.stroke-32");var subQ1=sQuery(id+"F0.wireOp",EDGE,"E11.sketch_text.stroke-31");var subQ2=makeQuery(id+"F0.imprint","INTERSECT",VERTEX,{"derivedFrom":[subQ1,subQ0]});Q82=makeQuery(id+"F0.imprint","IMPRINT",FACE,{"disambiguationData":[TD([[makeQuery(id+"F0.imprint","IMPRINT",EDGE,{"disambiguationData":[TD([[subQ2,1.0]])],"derivedFrom":subQ1}),-1.0]])]});}
            var Q83;
            {var subQ0=sQuery(id+"F0.wireOp",EDGE,"E11.sketch_text.stroke-26");var subQ1=sQuery(id+"F0.wireOp",EDGE,"E11.sketch_text.stroke-25");var subQ2=makeQuery(id+"F0.imprint","INTERSECT",VERTEX,{"derivedFrom":[subQ1,subQ0]});Q83=makeQuery(id+"F0.imprint","IMPRINT",FACE,{"disambiguationData":[TD([[makeQuery(id+"F0.imprint","IMPRINT",EDGE,{"disambiguationData":[TD([[subQ2,1.0]])],"derivedFrom":subQ1}),-1.0]])]});}
            extrude(context, id + "F1", {"entities" : qUnion([Q0, Q1, Q2, Q3, Q4, Q5, Q6, Q7, Q8, Q9, Q10, Q11, Q12, Q13, Q14, Q15, Q16, Q17, Q18, Q19, Q20, Q21, Q22, Q23, Q24, Q25, Q26, Q27, Q28, Q29, Q30, Q31, Q32, Q33, Q34, Q35, Q36, Q37, Q38, Q39, Q40, Q41, Q42, Q43, Q44, Q45, Q46, Q47, Q48, Q49, Q50, Q51, Q52, Q53, Q54, Q55, Q56, Q57, Q58, Q59, Q60, Q61, Q62, Q63, Q64, Q65, Q66, Q67, Q68, Q69, Q70, Q71, Q72, Q73, Q74, Q75, Q76, Q77, Q78, Q79, Q80, Q81, Q82, Q83]), "oppositeDirection" : true, "depth" : 4 * mm});
        }
        {
            var Q0;
            {var subQ5=sQuery(id+"F0.wireOp",EDGE,"E5");var subQ6=sQuery(id+"F0.wireOp",EDGE,"E0");var subQ7=makeQuery(id+"F0.imprint","INTERSECT",VERTEX,{"disambiguationData":[OD(0.0)],"derivedFrom":[subQ6,subQ5]});Q0=makeQuery(id+"F0.imprint","IMPRINT",FACE,{"disambiguationData":[TD([[makeQuery(id+"F0.imprint","IMPRINT",EDGE,{"disambiguationData":[TD([[subQ7,-1.0]])],"derivedFrom":subQ6}),-1.0]])]});}
            var Q1;
            {var subQ0=sQuery(id+"F0.wireOp",EDGE,"E13");var subQ1=sQuery(id+"F0.wireOp",EDGE,"E0");var subQ2=makeQuery(id+"F0.imprint","INTERSECT",VERTEX,{"disambiguationData":[OD(0.0)],"derivedFrom":[subQ1,subQ0]});Q1=makeQuery(id+"F0.imprint","IMPRINT",FACE,{"disambiguationData":[TD([[makeQuery(id+"F0.imprint","IMPRINT",EDGE,{"disambiguationData":[TD([[subQ2,-1.0]])],"derivedFrom":subQ1}),-1.0]])]});}
            var Q2;
            {var subQ0=sQuery(id+"F0.wireOp",EDGE,"E14");var subQ1=sQuery(id+"F0.wireOp",EDGE,"E0");var subQ2=makeQuery(id+"F0.imprint","INTERSECT",VERTEX,{"disambiguationData":[OD(0.0)],"derivedFrom":[subQ1,subQ0]});Q2=makeQuery(id+"F0.imprint","IMPRINT",FACE,{"disambiguationData":[TD([[makeQuery(id+"F0.imprint","IMPRINT",EDGE,{"disambiguationData":[TD([[subQ2,-1.0]])],"derivedFrom":subQ1}),-1.0]])]});}
            var Q3;
            {var subQ0=sQuery(id+"F0.wireOp",EDGE,"E13");var subQ1=sQuery(id+"F0.wireOp",EDGE,"E0");var subQ2=makeQuery(id+"F0.imprint","INTERSECT",VERTEX,{"disambiguationData":[OD(1.0)],"derivedFrom":[subQ1,subQ0]});Q3=makeQuery(id+"F0.imprint","IMPRINT",FACE,{"disambiguationData":[TD([[makeQuery(id+"F0.imprint","IMPRINT",EDGE,{"disambiguationData":[TD([[subQ2,-1.0]])],"derivedFrom":subQ1}),-1.0]])]});}
            var Q4;
            {var subQ0=sQuery(id+"F0.wireOp",EDGE,"E14");var subQ1=sQuery(id+"F0.wireOp",EDGE,"E0");var subQ2=makeQuery(id+"F0.imprint","INTERSECT",VERTEX,{"disambiguationData":[OD(1.0)],"derivedFrom":[subQ1,subQ0]});Q4=makeQuery(id+"F0.imprint","IMPRINT",FACE,{"disambiguationData":[TD([[makeQuery(id+"F0.imprint","IMPRINT",EDGE,{"disambiguationData":[TD([[subQ2,-1.0]])],"derivedFrom":subQ1}),-1.0]])]});}
            var Q5;
            {var subQ0=sQuery(id+"F0.wireOp",EDGE,"E5");var subQ1=sQuery(id+"F0.wireOp",EDGE,"E0");var subQ2=makeQuery(id+"F0.imprint","INTERSECT",VERTEX,{"disambiguationData":[OD(1.0)],"derivedFrom":[subQ1,subQ0]});Q5=makeQuery(id+"F0.imprint","IMPRINT",FACE,{"disambiguationData":[TD([[makeQuery(id+"F0.imprint","IMPRINT",EDGE,{"disambiguationData":[TD([[subQ2,-1.0]])],"derivedFrom":subQ1}),-1.0]])]});}
            var Q6;
            {var subQ0=sQuery(id+"F0.wireOp",EDGE,"E9");var subQ1=sQuery(id+"F0.wireOp",EDGE,"E0");var subQ2=makeQuery(id+"F0.imprint","INTERSECT",VERTEX,{"disambiguationData":[OD(0.0)],"derivedFrom":[subQ1,subQ0]});Q6=makeQuery(id+"F0.imprint","IMPRINT",FACE,{"disambiguationData":[TD([[makeQuery(id+"F0.imprint","IMPRINT",EDGE,{"disambiguationData":[TD([[subQ2,1.0]])],"derivedFrom":subQ1}),-1.0]])]});}
            var Q7;
            {var subQ0=sQuery(id+"F0.wireOp",EDGE,"E1");var subQ1=sQuery(id+"F0.wireOp",EDGE,"E0");var subQ2=makeQuery(id+"F0.imprint","INTERSECT",VERTEX,{"disambiguationData":[OD(0.0)],"derivedFrom":[subQ1,subQ0]});Q7=makeQuery(id+"F0.imprint","IMPRINT",FACE,{"disambiguationData":[TD([[makeQuery(id+"F0.imprint","IMPRINT",EDGE,{"disambiguationData":[TD([[subQ2,1.0]])],"derivedFrom":subQ1}),-1.0]])]});}
            var Q8;
            {var subQ0=sQuery(id+"F0.wireOp",EDGE,"E1");var subQ1=sQuery(id+"F0.wireOp",EDGE,"E0");var subQ2=makeQuery(id+"F0.imprint","INTERSECT",VERTEX,{"disambiguationData":[OD(0.0)],"derivedFrom":[subQ1,subQ0]});Q8=makeQuery(id+"F0.imprint","IMPRINT",FACE,{"disambiguationData":[TD([[makeQuery(id+"F0.imprint","IMPRINT",EDGE,{"disambiguationData":[TD([[subQ2,-1.0]])],"derivedFrom":subQ1}),-1.0]])]});}
            var Q9;
            {var subQ0=sQuery(id+"F0.wireOp",EDGE,"E1");var subQ1=sQuery(id+"F0.wireOp",EDGE,"E0");var subQ2=makeQuery(id+"F0.imprint","INTERSECT",VERTEX,{"disambiguationData":[OD(0.0)],"derivedFrom":[subQ1,subQ0]});Q9=makeQuery(id+"F0.imprint","IMPRINT",FACE,{"disambiguationData":[TD([[makeQuery(id+"F0.imprint","IMPRINT",EDGE,{"disambiguationData":[TD([[subQ2,-1.0]])],"derivedFrom":subQ1}),1.0]])]});}
            var Q10;
            {var subQ0=sQuery(id+"F0.wireOp",EDGE,"E5");var subQ1=sQuery(id+"F0.wireOp",EDGE,"E0");var subQ2=makeQuery(id+"F0.imprint","INTERSECT",VERTEX,{"disambiguationData":[OD(1.0)],"derivedFrom":[subQ1,subQ0]});Q10=makeQuery(id+"F0.imprint","IMPRINT",FACE,{"disambiguationData":[TD([[makeQuery(id+"F0.imprint","IMPRINT",EDGE,{"disambiguationData":[TD([[subQ2,-1.0]])],"derivedFrom":subQ1}),1.0]])]});}
            var Q11;
            {var subQ0=sQuery(id+"F0.wireOp",EDGE,"E4");var subQ1=sQuery(id+"F0.wireOp",EDGE,"E1");var subQ2=makeQuery(id+"F0.imprint","INTERSECT",VERTEX,{"disambiguationData":[OD(1.0)],"derivedFrom":[subQ1,subQ0]});Q11=makeQuery(id+"F0.imprint","IMPRINT",FACE,{"disambiguationData":[TD([[makeQuery(id+"F0.imprint","IMPRINT",EDGE,{"disambiguationData":[TD([[subQ2,-1.0]])],"derivedFrom":subQ1}),-1.0]])]});}
            var Q12;
            {var subQ0=sQuery(id+"F0.wireOp",EDGE,"E6");var subQ1=sQuery(id+"F0.wireOp",EDGE,"E1");var subQ2=makeQuery(id+"F0.imprint","INTERSECT",VERTEX,{"disambiguationData":[OD(1.0)],"derivedFrom":[subQ1,subQ0]});Q12=makeQuery(id+"F0.imprint","IMPRINT",FACE,{"disambiguationData":[TD([[makeQuery(id+"F0.imprint","IMPRINT",EDGE,{"disambiguationData":[TD([[subQ2,-1.0]])],"derivedFrom":subQ1}),-1.0]])]});}
            var Q13;
            {var subQ0=sQuery(id+"F0.wireOp",EDGE,"E9");var subQ1=sQuery(id+"F0.wireOp",EDGE,"E1");var subQ2=makeQuery(id+"F0.imprint","INTERSECT",VERTEX,{"disambiguationData":[OD(0.0)],"derivedFrom":[subQ1,subQ0]});Q13=makeQuery(id+"F0.imprint","IMPRINT",FACE,{"disambiguationData":[TD([[makeQuery(id+"F0.imprint","IMPRINT",EDGE,{"disambiguationData":[TD([[subQ2,1.0]])],"derivedFrom":subQ1}),-1.0]])]});}
            var Q14;
            {var subQ0=sQuery(id+"F0.wireOp",EDGE,"E6");var subQ1=sQuery(id+"F0.wireOp",EDGE,"E1");var subQ2=makeQuery(id+"F0.imprint","INTERSECT",VERTEX,{"disambiguationData":[OD(1.0)],"derivedFrom":[subQ1,subQ0]});Q14=makeQuery(id+"F0.imprint","IMPRINT",FACE,{"disambiguationData":[TD([[makeQuery(id+"F0.imprint","IMPRINT",EDGE,{"disambiguationData":[TD([[subQ2,-1.0]])],"derivedFrom":subQ1}),1.0]])]});}
            var Q15;
            {var subQ0=sQuery(id+"F0.wireOp",EDGE,"E2");var subQ1=sQuery(id+"F0.wireOp",EDGE,"E1");var subQ2=makeQuery(id+"F0.imprint","INTERSECT",VERTEX,{"disambiguationData":[OD(0.0)],"derivedFrom":[subQ1,subQ0]});Q15=makeQuery(id+"F0.imprint","IMPRINT",FACE,{"disambiguationData":[TD([[makeQuery(id+"F0.imprint","IMPRINT",EDGE,{"disambiguationData":[TD([[subQ2,-1.0]])],"derivedFrom":subQ1}),1.0]])]});}
            var Q16;
            {var subQ0=sQuery(id+"F0.wireOp",EDGE,"E2");var subQ1=sQuery(id+"F0.wireOp",EDGE,"E1");var subQ2=makeQuery(id+"F0.imprint","INTERSECT",VERTEX,{"disambiguationData":[OD(0.0)],"derivedFrom":[subQ1,subQ0]});Q16=makeQuery(id+"F0.imprint","IMPRINT",FACE,{"disambiguationData":[TD([[makeQuery(id+"F0.imprint","IMPRINT",EDGE,{"disambiguationData":[TD([[subQ2,-1.0]])],"derivedFrom":subQ1}),-1.0]])]});}
            var Q17;
            {var subQ0=sQuery(id+"F0.wireOp",EDGE,"E2");var subQ1=sQuery(id+"F0.wireOp",EDGE,"E1");var subQ2=makeQuery(id+"F0.imprint","INTERSECT",VERTEX,{"disambiguationData":[OD(0.0)],"derivedFrom":[subQ1,subQ0]});Q17=makeQuery(id+"F0.imprint","IMPRINT",FACE,{"disambiguationData":[TD([[makeQuery(id+"F0.imprint","IMPRINT",EDGE,{"disambiguationData":[TD([[subQ2,1.0]])],"derivedFrom":subQ1}),-1.0]])]});}
            var Q18;
            {var subQ6=sQuery(id+"F0.wireOp",EDGE,"E6");var subQ8=sQuery(id+"F0.wireOp",EDGE,"E1");var subQ10=makeQuery(id+"F0.imprint","INTERSECT",VERTEX,{"disambiguationData":[OD(0.0)],"derivedFrom":[subQ8,subQ6]});Q18=makeQuery(id+"F0.imprint","IMPRINT",FACE,{"disambiguationData":[TD([[makeQuery(id+"F0.imprint","IMPRINT",EDGE,{"disambiguationData":[TD([[subQ10,-1.0]])],"derivedFrom":subQ8}),-1.0]])]});}
            var Q19;
            {var subQ3=sQuery(id+"F0.wireOp",EDGE,"E7");var subQ5=sQuery(id+"F0.wireOp",EDGE,"E2");var subQ6=makeQuery(id+"F0.imprint","INTERSECT",VERTEX,{"disambiguationData":[OD(0.0)],"derivedFrom":[subQ5,subQ3]});Q19=makeQuery(id+"F0.imprint","IMPRINT",FACE,{"disambiguationData":[TD([[makeQuery(id+"F0.imprint","IMPRINT",EDGE,{"disambiguationData":[TD([[subQ6,-1.0]])],"derivedFrom":subQ5}),-1.0]])]});}
            var Q20;
            {var subQ0=sQuery(id+"F0.wireOp",EDGE,"E3");var subQ1=sQuery(id+"F0.wireOp",EDGE,"E2");var subQ2=makeQuery(id+"F0.imprint","INTERSECT",VERTEX,{"disambiguationData":[OD(0.0)],"derivedFrom":[subQ1,subQ0]});Q20=makeQuery(id+"F0.imprint","IMPRINT",FACE,{"disambiguationData":[TD([[makeQuery(id+"F0.imprint","IMPRINT",EDGE,{"disambiguationData":[TD([[subQ2,1.0]])],"derivedFrom":subQ1}),-1.0]])]});}
            var Q21;
            {var subQ0=sQuery(id+"F0.wireOp",EDGE,"E9");var subQ1=sQuery(id+"F0.wireOp",EDGE,"E2");var subQ2=makeQuery(id+"F0.imprint","INTERSECT",VERTEX,{"disambiguationData":[OD(0.0)],"derivedFrom":[subQ1,subQ0]});Q21=makeQuery(id+"F0.imprint","IMPRINT",FACE,{"disambiguationData":[TD([[makeQuery(id+"F0.imprint","IMPRINT",EDGE,{"disambiguationData":[TD([[subQ2,1.0]])],"derivedFrom":subQ1}),-1.0]])]});}
            var Q22;
            {var subQ0=sQuery(id+"F0.wireOp",EDGE,"E7");var subQ1=sQuery(id+"F0.wireOp",EDGE,"E2");var subQ2=makeQuery(id+"F0.imprint","INTERSECT",VERTEX,{"disambiguationData":[OD(1.0)],"derivedFrom":[subQ1,subQ0]});Q22=makeQuery(id+"F0.imprint","IMPRINT",FACE,{"disambiguationData":[TD([[makeQuery(id+"F0.imprint","IMPRINT",EDGE,{"disambiguationData":[TD([[subQ2,-1.0]])],"derivedFrom":subQ1}),-1.0]])]});}
            var Q23;
            {var subQ0=sQuery(id+"F0.wireOp",EDGE,"E5");var subQ1=sQuery(id+"F0.wireOp",EDGE,"E2");var subQ2=makeQuery(id+"F0.imprint","INTERSECT",VERTEX,{"disambiguationData":[OD(1.0)],"derivedFrom":[subQ1,subQ0]});Q23=makeQuery(id+"F0.imprint","IMPRINT",FACE,{"disambiguationData":[TD([[makeQuery(id+"F0.imprint","IMPRINT",EDGE,{"disambiguationData":[TD([[subQ2,-1.0]])],"derivedFrom":subQ1}),-1.0]])]});}
            var Q24;
            {var subQ0=sQuery(id+"F0.wireOp",EDGE,"E3");var subQ1=sQuery(id+"F0.wireOp",EDGE,"E2");var subQ2=makeQuery(id+"F0.imprint","INTERSECT",VERTEX,{"disambiguationData":[OD(0.0)],"derivedFrom":[subQ1,subQ0]});Q24=makeQuery(id+"F0.imprint","IMPRINT",FACE,{"disambiguationData":[TD([[makeQuery(id+"F0.imprint","IMPRINT",EDGE,{"disambiguationData":[TD([[subQ2,-1.0]])],"derivedFrom":subQ1}),-1.0]])]});}
            var Q25;
            {var subQ0=sQuery(id+"F0.wireOp",EDGE,"E3");var subQ1=sQuery(id+"F0.wireOp",EDGE,"E2");var subQ2=makeQuery(id+"F0.imprint","INTERSECT",VERTEX,{"disambiguationData":[OD(0.0)],"derivedFrom":[subQ1,subQ0]});Q25=makeQuery(id+"F0.imprint","IMPRINT",FACE,{"disambiguationData":[TD([[makeQuery(id+"F0.imprint","IMPRINT",EDGE,{"disambiguationData":[TD([[subQ2,-1.0]])],"derivedFrom":subQ1}),1.0]])]});}
            var Q26;
            {var subQ0=sQuery(id+"F0.wireOp",EDGE,"E7");var subQ1=sQuery(id+"F0.wireOp",EDGE,"E2");var subQ2=makeQuery(id+"F0.imprint","INTERSECT",VERTEX,{"disambiguationData":[OD(1.0)],"derivedFrom":[subQ1,subQ0]});Q26=makeQuery(id+"F0.imprint","IMPRINT",FACE,{"disambiguationData":[TD([[makeQuery(id+"F0.imprint","IMPRINT",EDGE,{"disambiguationData":[TD([[subQ2,-1.0]])],"derivedFrom":subQ1}),1.0]])]});}
            var Q27;
            {var subQ0=sQuery(id+"F0.wireOp",EDGE,"E9");var subQ1=sQuery(id+"F0.wireOp",EDGE,"E3");var subQ2=makeQuery(id+"F0.imprint","INTERSECT",VERTEX,{"disambiguationData":[OD(0.0)],"derivedFrom":[subQ1,subQ0]});Q27=makeQuery(id+"F0.imprint","IMPRINT",FACE,{"disambiguationData":[TD([[makeQuery(id+"F0.imprint","IMPRINT",EDGE,{"disambiguationData":[TD([[subQ2,1.0]])],"derivedFrom":subQ1}),-1.0]])]});}
            var Q28;
            {var subQ0=sQuery(id+"F0.wireOp",EDGE,"E6");var subQ1=sQuery(id+"F0.wireOp",EDGE,"E3");var subQ2=makeQuery(id+"F0.imprint","INTERSECT",VERTEX,{"disambiguationData":[OD(0.0)],"derivedFrom":[subQ1,subQ0]});Q28=makeQuery(id+"F0.imprint","IMPRINT",FACE,{"disambiguationData":[TD([[makeQuery(id+"F0.imprint","IMPRINT",EDGE,{"disambiguationData":[TD([[subQ2,1.0]])],"derivedFrom":subQ1}),-1.0]])]});}
            var Q29;
            {var subQ5=sQuery(id+"F0.wireOp",EDGE,"E11.sketch_text.stroke-0");Q29=makeQuery(id+"F0.imprint","IMPRINT",FACE,{"disambiguationData":[TD([[makeQuery(id+"F0.imprint","IMPRINT",EDGE,{"derivedFrom":subQ5}),-1.0]])]});}
            var Q30;
            Q30=makeQuery(id+"F0.imprint","IMPRINT",FACE,{"disambiguationData":[TD([[makeQuery(id+"F0.imprint","IMPRINT",EDGE,{"derivedFrom":sQuery(id+"F0.wireOp",EDGE,"E11.sketch_text.stroke-13")}),-1.0]])]});
            var Q31;
            {var subQ2=sQuery(id+"F0.wireOp",EDGE,"E11.sketch_text.stroke-30");Q31=makeQuery(id+"F0.imprint","IMPRINT",FACE,{"disambiguationData":[TD([[makeQuery(id+"F0.imprint","IMPRINT",EDGE,{"derivedFrom":subQ2}),-1.0]])]});}
            var Q32;
            {var subQ0=sQuery(id+"F0.wireOp",EDGE,"E11.sketch_text.stroke-55");Q32=makeQuery(id+"F0.imprint","IMPRINT",FACE,{"disambiguationData":[TD([[makeQuery(id+"F0.imprint","IMPRINT",EDGE,{"derivedFrom":subQ0}),-1.0]])]});}
            var Q33;
            {var subQ3=sQuery(id+"F0.wireOp",EDGE,"E11.sketch_text.stroke-66");Q33=makeQuery(id+"F0.imprint","IMPRINT",FACE,{"disambiguationData":[TD([[makeQuery(id+"F0.imprint","IMPRINT",EDGE,{"derivedFrom":subQ3}),-1.0]])]});}
            var Q34;
            Q34=makeQuery(id+"F0.imprint","IMPRINT",FACE,{"disambiguationData":[TD([[makeQuery(id+"F0.imprint","IMPRINT",EDGE,{"derivedFrom":sQuery(id+"F0.wireOp",EDGE,"E11.sketch_text.stroke-84")}),-1.0]])]});
            var Q35;
            {var subQ0=sQuery(id+"F0.wireOp",EDGE,"E9");var subQ1=sQuery(id+"F0.wireOp",EDGE,"E0");var subQ2=makeQuery(id+"F0.imprint","INTERSECT",VERTEX,{"disambiguationData":[OD(1.0)],"derivedFrom":[subQ1,subQ0]});Q35=makeQuery(id+"F0.imprint","IMPRINT",FACE,{"disambiguationData":[TD([[makeQuery(id+"F0.imprint","IMPRINT",EDGE,{"disambiguationData":[TD([[subQ2,-1.0]])],"derivedFrom":subQ1}),-1.0]])]});}
            extrude(context, id + "F2", {"entities" : qUnion([Q0, Q1, Q2, Q3, Q4, Q5, Q6, Q7, Q8, Q9, Q10, Q11, Q12, Q13, Q14, Q15, Q16, Q17, Q18, Q19, Q20, Q21, Q22, Q23, Q24, Q25, Q26, Q27, Q28, Q29, Q30, Q31, Q32, Q33, Q34, Q35]), "operationType" : NewBodyOperationType.ADD, "depth" : 4 * mm});
        }
    });
